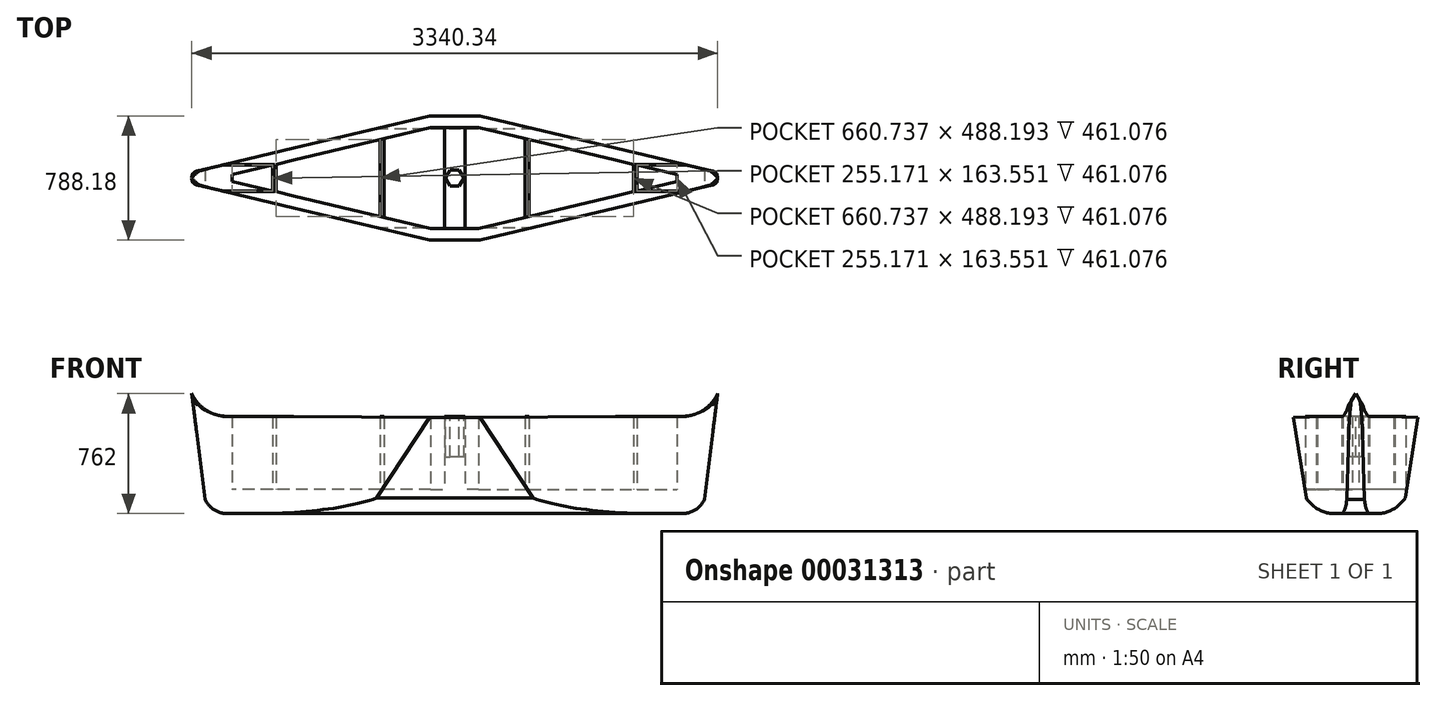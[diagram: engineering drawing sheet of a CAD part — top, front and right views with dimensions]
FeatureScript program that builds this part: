
annotation { "Feature Type Name" : "Feature", "Feature Type Description" : "" }
export const myFeature = defineFeature(function(context is Context, id is Id, definition is map)
    precondition{}
    {
        {
            var Q0;
            Q0=qCreatedBy(makeId("Top.planeOp"),FACE);
            var sketch = newSketch(context, id + "F0", { "sketchPlane" : qUnion([Q0])});
            skLineSegment(sketch, "E0", {"start": v(0, 396) * mm, "end": v(0, 0) * mm});
            skLineSegment(sketch, "E1", {"start": v(0, -396) * mm, "end": v(-152.4, -396) * mm});
            skLineSegment(sketch, "E2.MirrorCS", {"start": v(0, -396) * mm, "end": v(152.4, -396) * mm});
            skLineSegment(sketch, "E3", {"start": v(0, 396) * mm, "end": v(-152.4, 396) * mm});
            skLineSegment(sketch, "E4", {"start": v(-152.4, 396) * mm, "end": v(0, 396) * mm});
            skLineSegment(sketch, "E5", {"start": v(0, 396) * mm, "end": v(152.4, 396) * mm});
            skLineSegment(sketch, "E6", {"start": v(0, 0) * mm, "end": v(-1675, 0) * mm});
            skLineSegment(sketch, "E7", {"start": v(0, 0) * mm, "end": v(1675, 0) * mm});
            skLineSegment(sketch, "E8", {"start": v(0, 0) * mm, "end": v(0, -396) * mm});
            skLineSegment(sketch, "E9", {"start": v(-152.4, 396) * mm, "end": v(-1640.24, 42.9) * mm});
            skLineSegment(sketch, "E10.MirrorCS", {"start": v(-152.4, -396) * mm, "end": v(-1640.24, -42.9) * mm});
            skLineSegment(sketch, "E11.MirrorCS", {"start": v(152.4, 396) * mm, "end": v(1640.24, 42.9) * mm});
            skLineSegment(sketch, "E12.MirrorCS", {"start": v(152.4, -396) * mm, "end": v(1640.24, -42.9) * mm});
            skArc(sketch, "E13", {"start": v(-1640.24, 42.9) * mm, "mid": v(-1674.15, 0) * mm, "end": v(-1640.24, -42.9) * mm});
            skArc(sketch, "E14", {"start": v(1640.24, 42.9) * mm, "mid": v(1674.15, 0) * mm, "end": v(1640.24, -42.9) * mm});
            skLineSegment(sketch, "E15", {"start": v(-152.4, -320.3) * mm, "end": v(-1412.6, -21.22) * mm});
            skLineSegment(sketch, "E16", {"start": v(-1412.6, -21.22) * mm, "end": v(-1412.6, 0) * mm});
            skLineSegment(sketch, "E17", {"start": v(-152.4, -320.3) * mm, "end": v(0, -320.3) * mm});
            skLineSegment(sketch, "E18.MirrorCS", {"start": v(-152.4, 320.3) * mm, "end": v(0, 320.3) * mm});
            skLineSegment(sketch, "E19.MirrorCS", {"start": v(-152.4, 320.3) * mm, "end": v(-1412.6, 21.22) * mm});
            skLineSegment(sketch, "E20.MirrorCS", {"start": v(-1412.6, 21.22) * mm, "end": v(-1412.6, 0) * mm});
            skLineSegment(sketch, "E21.MirrorCS", {"start": v(152.4, 320.3) * mm, "end": v(1412.6, 21.22) * mm});
            skLineSegment(sketch, "E22.MirrorCS", {"start": v(152.4, 320.3) * mm, "end": v(0, 320.3) * mm});
            skLineSegment(sketch, "E23.MirrorCS", {"start": v(152.4, -320.3) * mm, "end": v(0, -320.3) * mm});
            skLineSegment(sketch, "E24.MirrorCS", {"start": v(152.4, -320.3) * mm, "end": v(1412.6, -21.22) * mm});
            skLineSegment(sketch, "E25.MirrorCS", {"start": v(1412.6, 21.22) * mm, "end": v(1412.6, 0) * mm});
            skLineSegment(sketch, "E26.MirrorCS", {"start": v(1412.6, -21.22) * mm, "end": v(1412.6, 0) * mm});
            skLineSegment(sketch, "E27", {"start": v(-64.2, 320.3) * mm, "end": v(-64.2, 0) * mm});
            skLineSegment(sketch, "E28", {"start": v(-64.2, 0) * mm, "end": v(-64.2, -320.3) * mm});
            skLineSegment(sketch, "E29.MirrorCS", {"start": v(64.2, 320.3) * mm, "end": v(64.2, 0) * mm});
            skLineSegment(sketch, "E30.MirrorCS", {"start": v(64.2, 0) * mm, "end": v(64.2, -320.3) * mm});
            skLineSegment(sketch, "E31", {"start": v(-473.47, 244.1) * mm, "end": v(-473.47, -244.1) * mm});
            skLineSegment(sketch, "E32", {"start": v(-448.4, 250.04) * mm, "end": v(-448.4, -250.04) * mm});
            skLineSegment(sketch, "E33", {"start": v(-1134.2, 87.29) * mm, "end": v(-1134.2, -87.29) * mm});
            skLineSegment(sketch, "E34", {"start": v(-1157.42, 81.78) * mm, "end": v(-1157.42, -81.78) * mm});
            skLineSegment(sketch, "E35.MirrorCS", {"start": v(448.4, 250.04) * mm, "end": v(448.4, -250.04) * mm});
            skLineSegment(sketch, "E36.MirrorCS", {"start": v(473.47, 244.1) * mm, "end": v(473.47, -244.1) * mm});
            skLineSegment(sketch, "E37.MirrorCS", {"start": v(1134.2, 87.29) * mm, "end": v(1134.2, -87.29) * mm});
            skLineSegment(sketch, "E38.MirrorCS", {"start": v(1157.42, 81.78) * mm, "end": v(1157.42, -81.78) * mm});
            skSolve(sketch);
        }
        {
            var Q0;
            Q0 = qSketchRegion(id + "F0", true);
            extrude(context, id + "F1", {"entities" : qUnion([Q0]), "depth" : 762 * mm});
        }
        {
            var Q0;
            Q0=qCreatedBy(makeId("Front.planeOp"),FACE);
            var sketch = newSketch(context, id + "F2", { "sketchPlane" : qUnion([Q0])});
            skLineSegment(sketch, "E39", {"start": v(-1446.66, 0) * mm, "end": v(0, 0) * mm});
            skLineSegment(sketch, "E40", {"start": v(-1446.66, 0) * mm, "end": v(-1446.66, 762) * mm});
            skArc(sketch, "E41", {"start": v(-1586.09, 89.4) * mm, "mid": v(-1529.47, 24.27) * mm, "end": v(-1446.66, 0) * mm});
            skLineSegment(sketch, "E42", {"start": v(-1586.09, 89.4) * mm, "end": v(-1670.17, 762) * mm});
            skArc(sketch, "E43", {"start": v(-1670.17, 762) * mm, "mid": v(-1579.55, 657.06) * mm, "end": v(-1446.66, 617.51) * mm});
            skLineSegment(sketch, "E44", {"start": v(-1446.66, 617.51) * mm, "end": v(0, 610.9) * mm});
            skLineSegment(sketch, "E45.MirrorCS", {"start": v(1446.66, 617.51) * mm, "end": v(0, 610.9) * mm});
            skLineSegment(sketch, "E46.MirrorCS", {"start": v(1446.66, 0) * mm, "end": v(0, 0) * mm});
            skArc(sketch, "E47.MirrorCS", {"start": v(1586.09, 89.4) * mm, "mid": v(1529.47, 24.27) * mm, "end": v(1446.66, 0) * mm});
            skLineSegment(sketch, "E48.MirrorCS", {"start": v(1586.09, 89.4) * mm, "end": v(1670.17, 762) * mm});
            skArc(sketch, "E49.MirrorCS", {"start": v(1670.17, 762) * mm, "mid": v(1579.55, 657.06) * mm, "end": v(1446.66, 617.51) * mm});
            skLineSegment(sketch, "E50.MirrorCS", {"start": v(1446.66, 0) * mm, "end": v(1446.66, 762) * mm});
            skSolve(sketch);
        }
        {
            var Q0;
            Q0 = qSketchRegion(id + "F2", true);
            extrude(context, id + "F3", {"entities" : qUnion([Q0]), "operationType" : NewBodyOperationType.INTERSECT, "endBound" : BoundingType.SYMMETRIC, "oppositeDirection" : true, "depth" : 6524.25 * mm});
        }
        {
            var Q0;
            Q0=qCreatedBy(makeId("Right.planeOp"),FACE);
            var sketch = newSketch(context, id + "F4", { "sketchPlane" : qUnion([Q0])});
            skLineSegment(sketch, "E51.bottom", {"start": v(394.7, 615.58) * mm, "end": v(85.2, 615.58) * mm});
            skLineSegment(sketch, "E51.top", {"start": v(394.7, 615.58) * mm, "end": v(85.2, 615.58) * mm});
            skLineSegment(sketch, "E51.left", {"start": v(394.7, 615.58) * mm, "end": v(394.7, 615.58) * mm});
            skLineSegment(sketch, "E51.right", {"start": v(85.2, 615.58) * mm, "end": v(85.2, 615.58) * mm});
            skLineSegment(sketch, "E52.MirrorCS", {"start": v(-394.7, 615.58) * mm, "end": v(-85.2, 615.58) * mm});
            skLineSegment(sketch, "E53", {"start": v(0, 0) * mm, "end": v(0, 762) * mm});
            skArc(sketch, "E54", {"start": v(46.37, 688.19) * mm, "mid": v(59.78, 648.67) * mm, "end": v(85.2, 615.58) * mm});
            skLineSegment(sketch, "E55", {"start": v(46.37, 688.19) * mm, "end": v(0, 762) * mm});
            skLineSegment(sketch, "E56.MirrorCS", {"start": v(-46.37, 688.19) * mm, "end": v(0, 762) * mm});
            skArc(sketch, "E57.MirrorCS", {"start": v(-46.37, 688.19) * mm, "mid": v(-59.78, 648.67) * mm, "end": v(-85.2, 615.58) * mm});
            skLineSegment(sketch, "E58", {"start": v(-394.7, 615.58) * mm, "end": v(-314.22, 98.76) * mm});
            skLineSegment(sketch, "E59.MirrorCS", {"start": v(394.7, 615.58) * mm, "end": v(314.22, 98.76) * mm});
            skArc(sketch, "E60", {"start": v(135.93, 0) * mm, "mid": v(237.7, 26.57) * mm, "end": v(314.22, 98.76) * mm});
            skLineSegment(sketch, "E61", {"start": v(135.93, 0) * mm, "end": v(0, 0) * mm});
            skLineSegment(sketch, "E62.MirrorCS", {"start": v(-135.93, 0) * mm, "end": v(0, 0) * mm});
            skArc(sketch, "E63.MirrorCS", {"start": v(-135.93, 0) * mm, "mid": v(-237.7, 26.57) * mm, "end": v(-314.22, 98.76) * mm});
            skSolve(sketch);
        }
        {
            var Q0;
            Q0 = qSketchRegion(id + "F4", true);
            extrude(context, id + "F5", {"entities" : qUnion([Q0]), "operationType" : NewBodyOperationType.INTERSECT, "endBound" : BoundingType.SYMMETRIC, "oppositeDirection" : true, "depth" : 11265.73 * mm});
        }
        {
            var Q0;
            {var subQ1=sQuery(id+"F0.wireOp",EDGE,"E6");var subQ5=sQuery(id+"F0.wireOp",EDGE,"E33");var subQ6=makeQuery(id+"F0.imprint","INTERSECT",VERTEX,{"derivedFrom":[subQ1,subQ5]});Q0=makeQuery(id+"F0.imprint","IMPRINT",FACE,{"disambiguationData":[TD([[makeQuery(id+"F0.imprint","IMPRINT",EDGE,{"disambiguationData":[TD([[subQ6,-1.0]])],"derivedFrom":subQ1}),-1.0]])]});}
            var Q1;
            {var subQ1=sQuery(id+"F0.wireOp",EDGE,"E6");var subQ5=sQuery(id+"F0.wireOp",EDGE,"E33");var subQ6=makeQuery(id+"F0.imprint","INTERSECT",VERTEX,{"derivedFrom":[subQ1,subQ5]});Q1=makeQuery(id+"F0.imprint","IMPRINT",FACE,{"disambiguationData":[TD([[makeQuery(id+"F0.imprint","IMPRINT",EDGE,{"disambiguationData":[TD([[subQ6,-1.0]])],"derivedFrom":subQ1}),1.0]])]});}
            var Q2;
            {var subQ0=sQuery(id+"F0.wireOp",EDGE,"E32");var subQ1=sQuery(id+"F0.wireOp",EDGE,"E6");var subQ2=makeQuery(id+"F0.imprint","INTERSECT",VERTEX,{"derivedFrom":[subQ1,subQ0]});Q2=makeQuery(id+"F0.imprint","IMPRINT",FACE,{"disambiguationData":[TD([[makeQuery(id+"F0.imprint","IMPRINT",EDGE,{"disambiguationData":[TD([[subQ2,-1.0]])],"derivedFrom":subQ1}),-1.0]])]});}
            var Q3;
            {var subQ0=sQuery(id+"F0.wireOp",EDGE,"E32");var subQ1=sQuery(id+"F0.wireOp",EDGE,"E6");var subQ2=makeQuery(id+"F0.imprint","INTERSECT",VERTEX,{"derivedFrom":[subQ1,subQ0]});Q3=makeQuery(id+"F0.imprint","IMPRINT",FACE,{"disambiguationData":[TD([[makeQuery(id+"F0.imprint","IMPRINT",EDGE,{"disambiguationData":[TD([[subQ2,-1.0]])],"derivedFrom":subQ1}),1.0]])]});}
            var Q4;
            {var subQ0=sQuery(id+"F0.wireOp",EDGE,"E29.MirrorCS");Q4=makeQuery(id+"F0.imprint","IMPRINT",FACE,{"disambiguationData":[TD([[makeQuery(id+"F0.imprint","IMPRINT",EDGE,{"derivedFrom":subQ0}),-1.0]])]});}
            var Q5;
            {var subQ0=sQuery(id+"F0.wireOp",EDGE,"E30.MirrorCS");Q5=makeQuery(id+"F0.imprint","IMPRINT",FACE,{"disambiguationData":[TD([[makeQuery(id+"F0.imprint","IMPRINT",EDGE,{"derivedFrom":subQ0}),-1.0]])]});}
            var Q6;
            {var subQ0=sQuery(id+"F0.wireOp",EDGE,"E28");Q6=makeQuery(id+"F0.imprint","IMPRINT",FACE,{"disambiguationData":[TD([[makeQuery(id+"F0.imprint","IMPRINT",EDGE,{"derivedFrom":subQ0}),1.0]])]});}
            var Q7;
            {var subQ0=sQuery(id+"F0.wireOp",EDGE,"E27");Q7=makeQuery(id+"F0.imprint","IMPRINT",FACE,{"disambiguationData":[TD([[makeQuery(id+"F0.imprint","IMPRINT",EDGE,{"derivedFrom":subQ0}),1.0]])]});}
            var Q8;
            {var subQ1=sQuery(id+"F0.wireOp",EDGE,"E7");var subQ5=sQuery(id+"F0.wireOp",EDGE,"E35.MirrorCS");var subQ7=makeQuery(id+"F0.imprint","INTERSECT",VERTEX,{"derivedFrom":[subQ1,subQ5]});Q8=makeQuery(id+"F0.imprint","IMPRINT",FACE,{"disambiguationData":[TD([[makeQuery(id+"F0.imprint","IMPRINT",EDGE,{"disambiguationData":[TD([[subQ7,-1.0]])],"derivedFrom":subQ1}),1.0]])]});}
            var Q9;
            {var subQ1=sQuery(id+"F0.wireOp",EDGE,"E7");var subQ5=sQuery(id+"F0.wireOp",EDGE,"E35.MirrorCS");var subQ6=makeQuery(id+"F0.imprint","INTERSECT",VERTEX,{"derivedFrom":[subQ1,subQ5]});Q9=makeQuery(id+"F0.imprint","IMPRINT",FACE,{"disambiguationData":[TD([[makeQuery(id+"F0.imprint","IMPRINT",EDGE,{"disambiguationData":[TD([[subQ6,-1.0]])],"derivedFrom":subQ1}),-1.0]])]});}
            var Q10;
            {var subQ1=sQuery(id+"F0.wireOp",EDGE,"E7");var subQ5=sQuery(id+"F0.wireOp",EDGE,"E37.MirrorCS");var subQ6=makeQuery(id+"F0.imprint","INTERSECT",VERTEX,{"derivedFrom":[subQ1,subQ5]});Q10=makeQuery(id+"F0.imprint","IMPRINT",FACE,{"disambiguationData":[TD([[makeQuery(id+"F0.imprint","IMPRINT",EDGE,{"disambiguationData":[TD([[subQ6,-1.0]])],"derivedFrom":subQ1}),1.0]])]});}
            var Q11;
            {var subQ1=sQuery(id+"F0.wireOp",EDGE,"E7");var subQ5=sQuery(id+"F0.wireOp",EDGE,"E37.MirrorCS");var subQ6=makeQuery(id+"F0.imprint","INTERSECT",VERTEX,{"derivedFrom":[subQ1,subQ5]});Q11=makeQuery(id+"F0.imprint","IMPRINT",FACE,{"disambiguationData":[TD([[makeQuery(id+"F0.imprint","IMPRINT",EDGE,{"disambiguationData":[TD([[subQ6,-1.0]])],"derivedFrom":subQ1}),-1.0]])]});}
            extrude(context, id + "F6", {"entities" : qUnion([Q0, Q1, Q2, Q3, Q4, Q5, Q6, Q7, Q8, Q9, Q10, Q11]), "operationType" : NewBodyOperationType.ADD, "depth" : 615.58 * mm});
        }
        {
            var Q0;
            {var subQ5=sQuery(id+"F0.wireOp",EDGE,"E27");Q0=makeQuery(id+"F0.imprint","IMPRINT",FACE,{"disambiguationData":[TD([[makeQuery(id+"F0.imprint","IMPRINT",EDGE,{"derivedFrom":subQ5}),-1.0]])]});}
            var Q1;
            {var subQ1=sQuery(id+"F0.wireOp",EDGE,"E6");var subQ5=sQuery(id+"F0.wireOp",EDGE,"E31");var subQ6=makeQuery(id+"F0.imprint","INTERSECT",VERTEX,{"derivedFrom":[subQ1,subQ5]});Q1=makeQuery(id+"F0.imprint","IMPRINT",FACE,{"disambiguationData":[TD([[makeQuery(id+"F0.imprint","IMPRINT",EDGE,{"disambiguationData":[TD([[subQ6,-1.0]])],"derivedFrom":subQ1}),-1.0]])]});}
            var Q2;
            {var subQ5=sQuery(id+"F0.wireOp",EDGE,"E20.MirrorCS");Q2=makeQuery(id+"F0.imprint","IMPRINT",FACE,{"disambiguationData":[TD([[makeQuery(id+"F0.imprint","IMPRINT",EDGE,{"derivedFrom":subQ5}),1.0]])]});}
            var Q3;
            {var subQ5=sQuery(id+"F0.wireOp",EDGE,"E16");Q3=makeQuery(id+"F0.imprint","IMPRINT",FACE,{"disambiguationData":[TD([[makeQuery(id+"F0.imprint","IMPRINT",EDGE,{"derivedFrom":subQ5}),-1.0]])]});}
            var Q4;
            {var subQ1=sQuery(id+"F0.wireOp",EDGE,"E6");var subQ5=sQuery(id+"F0.wireOp",EDGE,"E31");var subQ6=makeQuery(id+"F0.imprint","INTERSECT",VERTEX,{"derivedFrom":[subQ1,subQ5]});Q4=makeQuery(id+"F0.imprint","IMPRINT",FACE,{"disambiguationData":[TD([[makeQuery(id+"F0.imprint","IMPRINT",EDGE,{"disambiguationData":[TD([[subQ6,-1.0]])],"derivedFrom":subQ1}),1.0]])]});}
            var Q5;
            {var subQ5=sQuery(id+"F0.wireOp",EDGE,"E28");Q5=makeQuery(id+"F0.imprint","IMPRINT",FACE,{"disambiguationData":[TD([[makeQuery(id+"F0.imprint","IMPRINT",EDGE,{"derivedFrom":subQ5}),-1.0]])]});}
            var Q6;
            {var subQ6=sQuery(id+"F0.wireOp",EDGE,"E29.MirrorCS");Q6=makeQuery(id+"F0.imprint","IMPRINT",FACE,{"disambiguationData":[TD([[makeQuery(id+"F0.imprint","IMPRINT",EDGE,{"derivedFrom":subQ6}),1.0]])]});}
            var Q7;
            {var subQ5=sQuery(id+"F0.wireOp",EDGE,"E30.MirrorCS");Q7=makeQuery(id+"F0.imprint","IMPRINT",FACE,{"disambiguationData":[TD([[makeQuery(id+"F0.imprint","IMPRINT",EDGE,{"derivedFrom":subQ5}),1.0]])]});}
            var Q8;
            {var subQ1=sQuery(id+"F0.wireOp",EDGE,"E7");var subQ5=sQuery(id+"F0.wireOp",EDGE,"E36.MirrorCS");var subQ6=makeQuery(id+"F0.imprint","INTERSECT",VERTEX,{"derivedFrom":[subQ1,subQ5]});Q8=makeQuery(id+"F0.imprint","IMPRINT",FACE,{"disambiguationData":[TD([[makeQuery(id+"F0.imprint","IMPRINT",EDGE,{"disambiguationData":[TD([[subQ6,-1.0]])],"derivedFrom":subQ1}),-1.0]])]});}
            var Q9;
            {var subQ1=sQuery(id+"F0.wireOp",EDGE,"E7");var subQ5=sQuery(id+"F0.wireOp",EDGE,"E36.MirrorCS");var subQ6=makeQuery(id+"F0.imprint","INTERSECT",VERTEX,{"derivedFrom":[subQ1,subQ5]});Q9=makeQuery(id+"F0.imprint","IMPRINT",FACE,{"disambiguationData":[TD([[makeQuery(id+"F0.imprint","IMPRINT",EDGE,{"disambiguationData":[TD([[subQ6,-1.0]])],"derivedFrom":subQ1}),1.0]])]});}
            var Q10;
            {var subQ5=sQuery(id+"F0.wireOp",EDGE,"E25.MirrorCS");Q10=makeQuery(id+"F0.imprint","IMPRINT",FACE,{"disambiguationData":[TD([[makeQuery(id+"F0.imprint","IMPRINT",EDGE,{"derivedFrom":subQ5}),-1.0]])]});}
            var Q11;
            {var subQ5=sQuery(id+"F0.wireOp",EDGE,"E26.MirrorCS");Q11=makeQuery(id+"F0.imprint","IMPRINT",FACE,{"disambiguationData":[TD([[makeQuery(id+"F0.imprint","IMPRINT",EDGE,{"derivedFrom":subQ5}),1.0]])]});}
            extrude(context, id + "F7", {"entities" : qUnion([Q0, Q1, Q2, Q3, Q4, Q5, Q6, Q7, Q8, Q9, Q10, Q11]), "operationType" : NewBodyOperationType.ADD, "depth" : 154.5 * mm});
        }
        {
            var Q0;
            Q0 = qSketchRegion(id + "F4", true);
            extrude(context, id + "F8", {"entities" : qUnion([Q0]), "operationType" : NewBodyOperationType.INTERSECT, "endBound" : BoundingType.SYMMETRIC, "depth" : 10154.73 * mm});
        }
        {
            var Q0;
            Q0=makeQuery(id+"F6.opExtrude","CAP_FACE",FACE,{"disambiguationData":[OSD([sQuery(id+"F0.wireOp",EDGE,"E17"),sQuery(id+"F0.wireOp",EDGE,"E18.MirrorCS"),sQuery(id+"F0.wireOp",EDGE,"E22.MirrorCS"),sQuery(id+"F0.wireOp",EDGE,"E23.MirrorCS"),sQuery(id+"F0.wireOp",EDGE,"E27"),sQuery(id+"F0.wireOp",EDGE,"E28"),sQuery(id+"F0.wireOp",EDGE,"E29.MirrorCS"),sQuery(id+"F0.wireOp",EDGE,"E30.MirrorCS")])],"isStart":false});
            var sketch = newSketch(context, id + "F9", { "sketchPlane" : qUnion([Q0])});
            skCircle(sketch, "E64.cCircle", {"center": v(0, 0) * mm, "radius": 50.77 * mm, "construction": true});
            skLineSegment(sketch, "E64.0", {"start": v(29.31, -50.77) * mm, "end": v(-29.31, -50.77) * mm});
            skLineSegment(sketch, "E64.1", {"start": v(-29.31, -50.77) * mm, "end": v(-58.62, 0) * mm});
            skLineSegment(sketch, "E64.2", {"start": v(-58.62, 0) * mm, "end": v(-29.31, 50.77) * mm});
            skLineSegment(sketch, "E64.3", {"start": v(-29.31, 50.77) * mm, "end": v(29.31, 50.77) * mm});
            skLineSegment(sketch, "E64.4", {"start": v(29.31, 50.77) * mm, "end": v(58.62, 0) * mm});
            skLineSegment(sketch, "E64.5", {"start": v(58.62, 0) * mm, "end": v(29.31, -50.77) * mm});
            skPoint(sketch, "E64.0.midPoint", {"position": v(0, -50.77) * mm});
            skSolve(sketch);
        }
        {
            var Q0;
            Q0=makeQuery(id+"F9.imprint","IMPRINT",FACE,{"disambiguationData":[TD([[makeQuery(id+"F9.imprint","IMPRINT",EDGE,{"derivedFrom":sQuery(id+"F9.wireOp",EDGE,"E64.0")}),-1.0]])]});
            var Q1;
            Q1=sQuery(id+"F9.wireOp",EDGE,"E64.3");
            var Q2;
            Q2=sQuery(id+"F9.wireOp",EDGE,"E64.2");
            var Q3;
            Q3=sQuery(id+"F9.wireOp",EDGE,"E64.1");
            var Q4;
            Q4=sQuery(id+"F9.wireOp",EDGE,"E64.0");
            var Q5;
            Q5=sQuery(id+"F9.wireOp",EDGE,"E64.5");
            var Q6;
            Q6=sQuery(id+"F9.wireOp",EDGE,"E64.4");
            extrude(context, id + "F10", {"entities" : qUnion([Q0]), "operationType" : NewBodyOperationType.REMOVE, "surfaceEntities" : qUnion([Q1, Q2, Q3, Q4, Q5, Q6]), "oppositeDirection" : true, "depth" : 256.55 * mm});
        }
    });
